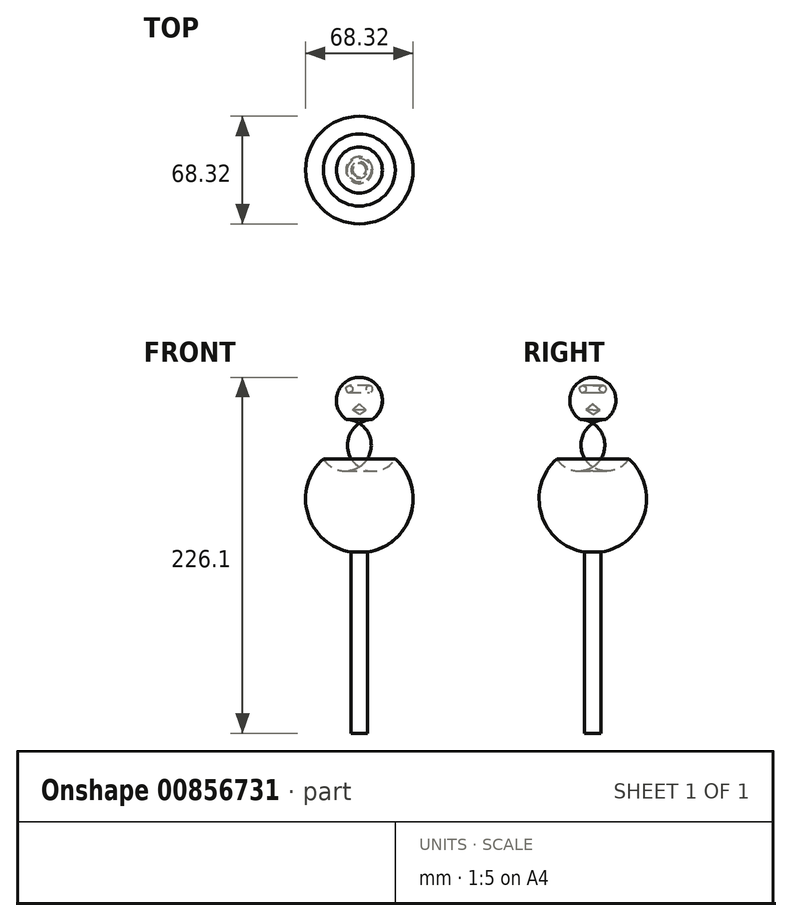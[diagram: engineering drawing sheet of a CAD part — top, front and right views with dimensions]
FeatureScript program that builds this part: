
annotation { "Feature Type Name" : "Feature", "Feature Type Description" : "" }
export const myFeature = defineFeature(function(context is Context, id is Id, definition is map)
    precondition{}
    {
        {
            var Q0;
            Q0=qCreatedBy(makeId("Top.planeOp"),FACE);
            var sketch = newSketch(context, id + "F0", { "sketchPlane" : qUnion([Q0])});
            skCircle(sketch, "E0", {"center": v(0, 0) * mm, "radius": 5.25 * mm});
            skSolve(sketch);
        }
        {
            var Q0;
            Q0 = qSketchRegion(id + "F0", true);
            extrude(context, id + "F1", {"entities" : qUnion([Q0]), "depth" : 150 * mm, "offsetDistance" : 25 * mm});
        }
        {
            var Q0;
            Q0=qCreatedBy(makeId("Front.planeOp"),FACE);
            var sketch = newSketch(context, id + "F2", { "sketchPlane" : qUnion([Q0])});
            skPoint(sketch, "E1.end.orphan", {"position": v(0, 135.44) * mm});
            skPoint(sketch, "E2.orphan", {"position": v(0, 114.74) * mm});
            skArc(sketch, "E3", {"start": v(0, 114.74) * mm, "mid": v(31.89, 136.65) * mm, "end": v(22.88, 174.27) * mm});
            skLineSegment(sketch, "E4", {"start": v(0, 114.74) * mm, "end": v(-17.88, 114.74) * mm, "construction": true});
            skLineSegment(sketch, "E5", {"start": v(0, 226.1) * mm, "end": v(-9.83, 226.1) * mm, "construction": true});
            skLineSegment(sketch, "E6", {"start": v(0, 226.1) * mm, "end": v(0, 114.74) * mm});
            skArc(sketch, "E7", {"start": v(22.88, 174.27) * mm, "mid": v(23.16, 191.24) * mm, "end": v(8.31, 199.45) * mm});
            skArc(sketch, "E8", {"start": v(8.31, 199.45) * mm, "mid": v(13.96, 215.83) * mm, "end": v(0, 226.1) * mm});
            skCircle(sketch, "E9", {"center": v(6.37, 218.6) * mm, "radius": 2.16 * mm});
            skCircle(sketch, "E10.MirrorC", {"center": v(-6.37, 218.6) * mm, "radius": 2.16 * mm});
            skLineSegment(sketch, "E11", {"start": v(0, 209) * mm, "end": v(4.38, 205.34) * mm});
            skLineSegment(sketch, "E12", {"start": v(4.38, 205.34) * mm, "end": v(0, 202.41) * mm});
            skLineSegment(sketch, "E13.MirrorCS", {"start": v(0, 209) * mm, "end": v(-4.38, 205.34) * mm});
            skLineSegment(sketch, "E14.MirrorCS", {"start": v(-4.38, 205.34) * mm, "end": v(0, 202.41) * mm});
            skSolve(sketch);
        }
        {
            var Q0;
            Q0=makeQuery(id+"F2.imprint","IMPRINT",FACE,{"disambiguationData":[TD([[makeQuery(id+"F2.imprint","IMPRINT",EDGE,{"derivedFrom":sQuery(id+"F2.wireOp",EDGE,"E3")}),1.0]])]});
            var Q1;
            Q1=sQuery(id+"F2.wireOp",EDGE,"E6");
            revolve(context, id + "F3", {"operationType" : NewBodyOperationType.ADD, "surfaceOperationType" : NewSurfaceOperationType.NEW, "entities" : qUnion([Q0]), "axis" : qUnion([Q1]), "revolveType" : RevolveType.FULL});
        }
        {
            var Q0;
            Q0=sQuery(id+"F2.wireOp",EDGE,"E9");
            extrude(context, id + "F4", {"bodyType" : ToolBodyType.SURFACE, "surfaceEntities" : qUnion([Q0]), "depth" : 13 * mm, "offsetDistance" : 25 * mm});
        }
        {
            var Q0;
            Q0=sQuery(id+"F2.wireOp",EDGE,"E10.MirrorC");
            extrude(context, id + "F5", {"bodyType" : ToolBodyType.SURFACE, "surfaceEntities" : qUnion([Q0]), "depth" : 13 * mm, "offsetDistance" : 25 * mm});
        }
    });
